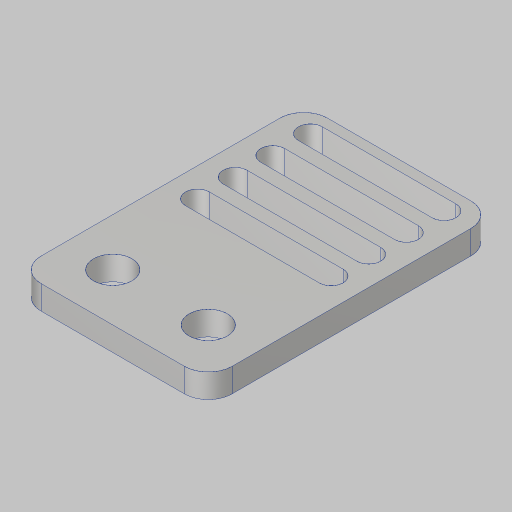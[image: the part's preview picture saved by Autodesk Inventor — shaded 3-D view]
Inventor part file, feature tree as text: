
AUTODESK INVENTOR PART (.ipt)
format: ipt  version: 2023.5 (Build 275446000, 446)  size: 154,112 bytes
history: native  units: in
note: dims shown in document units (in); Inventor stores cm internally (conversion verified against a paired STEP export)
features: sketch x1, extrude x1, hole x1, fillet x1
ambient origin geometry x8: Origin, YZ Plane, XZ Plane, XY Plane, X Axis, Y Axis, Z Axis, Center Point
bodies: Solid1 (feature_tree)
feature tree (4):
  sketch  "Sketch1"  dims[d1=0.7in d3=0.125in d4=0.197in d5=0.197in d8=1.0in d9=1.5in d10=0.25in d11=0.5in d12=0.25in d13=0.125in d14=0.0in d15=0.201in d16=0.75in d17=0.385in d18=0.25in d19=0.5635in d20=1.0in d21=0.8108in d22=0.125in d23=0.7874in d25=0.197in d26=0.3937in d28=1.0in]
  extrude  "Extrusion1"  Depth=0.125in
  hole  "Hole1"  [1 undecoded]
  fillet  "Fillet1"  Radius=0.197in
note: 1 required parameter value undecoded (feature->parameter linkage not recoverable at this tier; creation-order binding heuristic only, values carry confidence <= 0.55)
